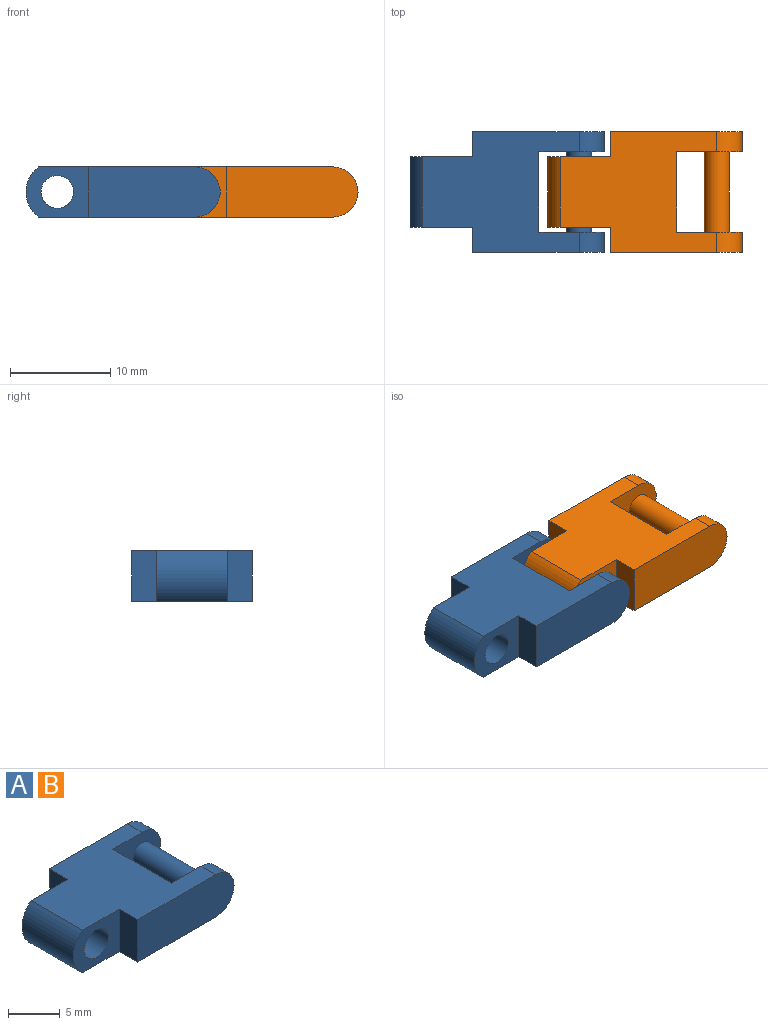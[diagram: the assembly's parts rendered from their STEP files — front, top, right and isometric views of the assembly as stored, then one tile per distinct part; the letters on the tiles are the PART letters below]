
ASSEMBLY  parts=2 mates=1
PART A: 16 faces, bbox 19.4x12x5 mm
  f0: plane 6.25x5mm, normal (0,1,0), area 21.1mm2, adj f5,f6,f10,f13,f14
  f1: plane 6.25x5mm, normal (0,-1,0), area 21.1mm2, adj f5,f6,f7,f13,f14
  f2: plane 6.5x5mm, normal (0,1,0), area 24.9mm2, adj f5,f6,f9,f12,f15
  f3: plane 6.5x5mm, normal (0,-1,0), area 24.9mm2, adj f5,f6,f9,f11,f15
  f4: plane 13.12x5mm, normal (0,1,0), area 62.9mm2, adj f5,f6,f10,f11
  f5: plane 15.62x12mm, normal (0,0,1), area 130.4mm2, adj f0,f1,f2,f3,f4,f7,f8,f9
  f6: plane 15.62x12mm, normal (0,0,-1), area 130.4mm2, adj f0,f1,f2,f3,f4,f7,f8,f9
  f7: plane 5x2.5mm, normal (-1,0,0), area 12.5mm2, adj f1,f5,f6,f8
  f8: plane 13.12x5mm, normal (0,-1,0), area 62.9mm2, adj f5,f6,f7,f12
  f9: plane 8x5mm, normal (1,0,0), area 40mm2, adj f2,f3,f5,f6
  f10: plane 5x2.5mm, normal (-1,0,0), area 12.5mm2, adj f0,f4,f5,f6
  f11: cylinder r=2.5mm len=5mm, axis (0,-1,0), area 15.7mm2, adj f3,f4,f5,f6
  f12: cylinder r=2.5mm len=5mm, axis (0,-1,0), area 15.7mm2, adj f2,f5,f6,f8
  f13: cylinder r=3.12mm len=7mm, axis (0,-1,0), area 40.6mm2, adj f0,f1,f5,f6
  f14: cylinder r=1.62mm len=7mm, axis (0,-1,0), area 71.5mm2, adj f0,f1
  f15: cylinder r=1.25mm len=8mm, axis (0,1,0), area 62.8mm2, adj f2,f3
PART B: same geometry as A
PLACE A t=(-12.13,6.16,-5.62)mm
PLACE B t=(1.62,6.16,-5.62)mm
MATE fastened A.f15 <-> B.f13  axis (0,1,0) through (18.1,12.16,-3.12)mm
